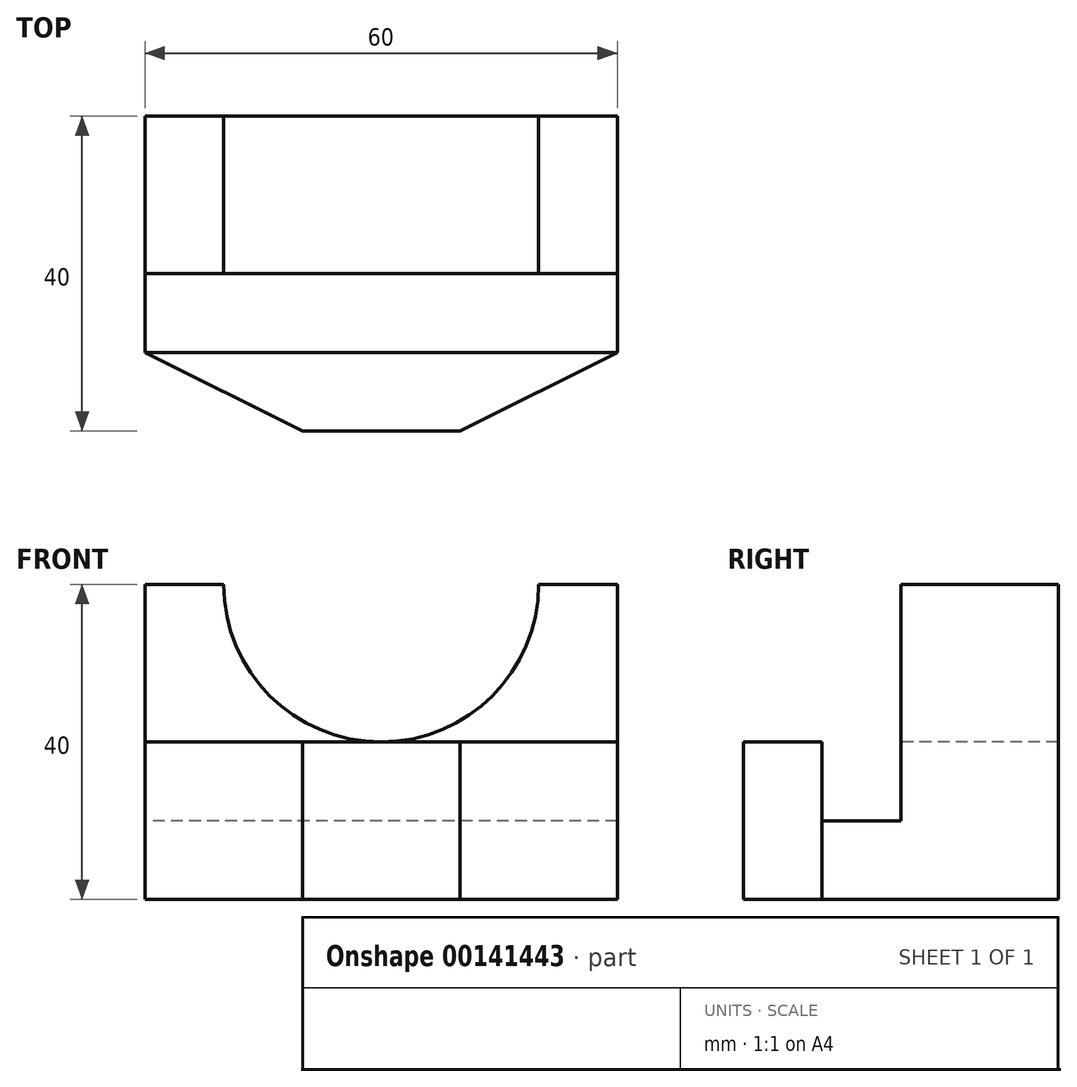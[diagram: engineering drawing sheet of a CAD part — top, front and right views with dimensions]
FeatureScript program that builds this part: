
annotation { "Feature Type Name" : "Feature", "Feature Type Description" : "" }
export const myFeature = defineFeature(function(context is Context, id is Id, definition is map)
    precondition{}
    {
        {
            var Q0;
            Q0=qCreatedBy(makeId("Right.planeOp"),FACE);
            var sketch = newSketch(context, id + "F0", { "sketchPlane" : qUnion([Q0])});
            skLineSegment(sketch, "E0.bottom", {"start": v(0, 0) * mm, "end": v(40, 0) * mm});
            skLineSegment(sketch, "E0.top", {"start": v(0, 40) * mm, "end": v(40, 40) * mm});
            skLineSegment(sketch, "E0.left", {"start": v(0, 0) * mm, "end": v(0, 40) * mm});
            skLineSegment(sketch, "E0.right", {"start": v(40, 0) * mm, "end": v(40, 40) * mm});
            skLineSegment(sketch, "E1", {"start": v(0, 20) * mm, "end": v(10, 20) * mm});
            skLineSegment(sketch, "E2", {"start": v(10, 20) * mm, "end": v(10, 0) * mm});
            skLineSegment(sketch, "E3", {"start": v(10, 10) * mm, "end": v(20, 10) * mm});
            skLineSegment(sketch, "E4", {"start": v(20, 10) * mm, "end": v(20, 40) * mm});
            skSolve(sketch);
        }
        {
            var Q0;
            {var subQ1=sQuery(id+"F0.wireOp",EDGE,"E1");Q0=makeQuery(id+"F0.imprint","IMPRINT",FACE,{"disambiguationData":[TD([[makeQuery(id+"F0.imprint","IMPRINT",EDGE,{"derivedFrom":subQ1}),-1.0]])]});}
            var Q1;
            {var subQ4=sQuery(id+"F0.wireOp",EDGE,"E0.right");Q1=makeQuery(id+"F0.imprint","IMPRINT",FACE,{"disambiguationData":[TD([[makeQuery(id+"F0.imprint","IMPRINT",EDGE,{"derivedFrom":subQ4}),1.0]])]});}
            extrude(context, id + "F1", {"entities" : qUnion([Q0, Q1]), "depth" : 60 * mm});
        }
        {
            var Q0;
            Q0=makeQuery(id+"F1.opExtrude","SWEPT_FACE",FACE,{"disambiguationData":[OSD([sQuery(id+"F0.wireOp",EDGE,"E1")])]});
            var sketch = newSketch(context, id + "F2", { "sketchPlane" : qUnion([Q0])});
            skLineSegment(sketch, "E5", {"start": v(0, 10) * mm, "end": v(20, 0) * mm});
            skLineSegment(sketch, "E6", {"start": v(60, 10) * mm, "end": v(40, 0) * mm});
            skLineSegment(sketch, "E7.0", {"start": v(60, 10) * mm, "end": v(0, 10) * mm});
            skLineSegment(sketch, "E8.0", {"start": v(60, 0) * mm, "end": v(0, 0) * mm});
            skLineSegment(sketch, "E9.0", {"start": v(0, 0) * mm, "end": v(0, 10) * mm});
            skLineSegment(sketch, "E10.0", {"start": v(60, 0) * mm, "end": v(60, 10) * mm});
            skSolve(sketch);
        }
        {
            var Q0;
            {var subQ0=sQuery(id+"F2.wireOp",EDGE,"E5");Q0=makeQuery(id+"F2.imprint","IMPRINT",FACE,{"disambiguationData":[TD([[makeQuery(id+"F2.imprint","IMPRINT",EDGE,{"derivedFrom":subQ0}),-1.0]])]});}
            var Q1;
            {var subQ0=sQuery(id+"F2.wireOp",EDGE,"E6");Q1=makeQuery(id+"F2.imprint","IMPRINT",FACE,{"disambiguationData":[TD([[makeQuery(id+"F2.imprint","IMPRINT",EDGE,{"derivedFrom":subQ0}),1.0]])]});}
            extrude(context, id + "F3", {"entities" : qUnion([Q0, Q1]), "operationType" : NewBodyOperationType.REMOVE, "endBound" : BoundingType.THROUGH_ALL, "oppositeDirection" : true, "depth" : 25 * mm});
        }
        {
            var Q0;
            Q0=makeQuery(id+"F1.opExtrude","SWEPT_FACE",FACE,{"disambiguationData":[OSD([sQuery(id+"F0.wireOp",EDGE,"E4")])]});
            var sketch = newSketch(context, id + "F4", { "sketchPlane" : qUnion([Q0])});
            skLineSegment(sketch, "E11.0.0", {"start": v(0, 40) * mm, "end": v(0, 10) * mm});
            skLineSegment(sketch, "E11.0.1", {"start": v(0, 10) * mm, "end": v(60, 10) * mm});
            skLineSegment(sketch, "E11.0.2", {"start": v(60, 10) * mm, "end": v(60, 40) * mm});
            skLineSegment(sketch, "E11.0.3", {"start": v(60, 40) * mm, "end": v(0, 40) * mm});
            skLineSegment(sketch, "E12.0.0", {"start": v(0, 0) * mm, "end": v(20, 0) * mm});
            skLineSegment(sketch, "E12.0.1", {"start": v(20, 0) * mm, "end": v(20, 20) * mm});
            skLineSegment(sketch, "E12.0.2", {"start": v(20, 20) * mm, "end": v(0, 20) * mm});
            skLineSegment(sketch, "E12.0.3", {"start": v(0, 20) * mm, "end": v(0, 10) * mm});
            skLineSegment(sketch, "E12.0.4", {"start": v(0, 10) * mm, "end": v(0, 0) * mm});
            skLineSegment(sketch, "E13.0.0", {"start": v(20, 0) * mm, "end": v(40, 0) * mm});
            skLineSegment(sketch, "E13.0.1", {"start": v(40, 0) * mm, "end": v(40, 20) * mm});
            skLineSegment(sketch, "E13.0.2", {"start": v(40, 20) * mm, "end": v(20, 20) * mm});
            skLineSegment(sketch, "E13.0.3", {"start": v(20, 20) * mm, "end": v(20, 0) * mm});
            skLineSegment(sketch, "E14.0.0", {"start": v(60, 0) * mm, "end": v(60, 10) * mm});
            skLineSegment(sketch, "E14.0.1", {"start": v(60, 10) * mm, "end": v(60, 20) * mm});
            skLineSegment(sketch, "E14.0.2", {"start": v(60, 20) * mm, "end": v(40, 20) * mm});
            skLineSegment(sketch, "E14.0.3", {"start": v(40, 20) * mm, "end": v(40, 0) * mm});
            skLineSegment(sketch, "E14.0.4", {"start": v(40, 0) * mm, "end": v(60, 0) * mm});
            skLineSegment(sketch, "E15", {"start": v(0, 0) * mm, "end": v(0, 20) * mm});
            skLineSegment(sketch, "E16", {"start": v(0, 40) * mm, "end": v(10, 40) * mm});
            skLineSegment(sketch, "E17", {"start": v(60, 40) * mm, "end": v(50, 40) * mm});
            skArc(sketch, "E18", {"start": v(10, 40) * mm, "mid": v(30, 20) * mm, "end": v(50, 40) * mm});
            skSolve(sketch);
        }
        {
            var Q0;
            {var subQ0=sQuery(id+"F4.wireOp",EDGE,"E11.0.3");Q0=makeQuery(id+"F4.imprint","IMPRINT",FACE,{"disambiguationData":[TD([[makeQuery(id+"F4.imprint","IMPRINT",EDGE,{"derivedFrom":subQ0}),1.0]])]});}
            extrude(context, id + "F5", {"entities" : qUnion([Q0]), "operationType" : NewBodyOperationType.REMOVE, "endBound" : BoundingType.THROUGH_ALL, "oppositeDirection" : true, "depth" : 25 * mm});
        }
    });
